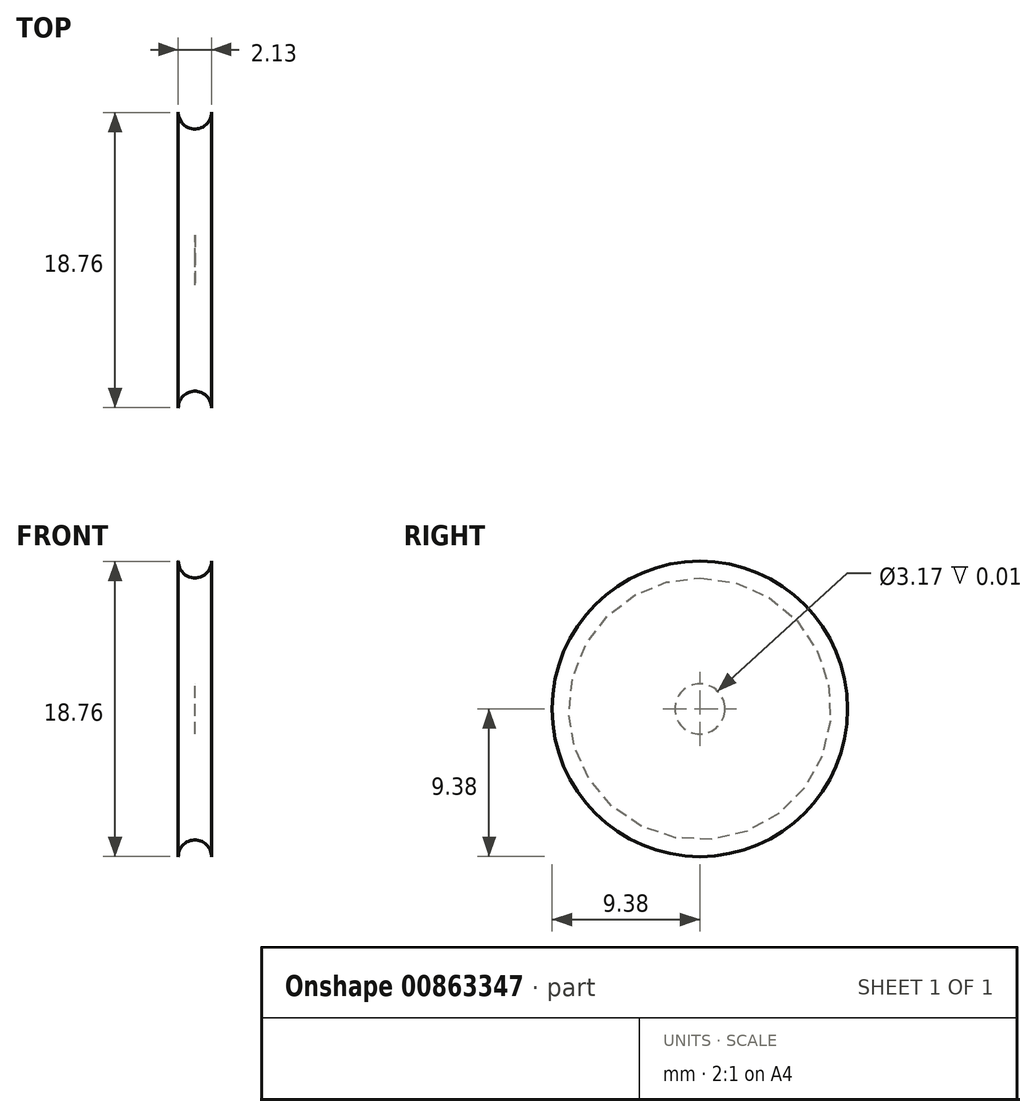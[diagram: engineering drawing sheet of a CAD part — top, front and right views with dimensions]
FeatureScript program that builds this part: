
annotation { "Feature Type Name" : "Feature", "Feature Type Description" : "" }
export const myFeature = defineFeature(function(context is Context, id is Id, definition is map)
    precondition{}
    {
        {
            var Q0;
            Q0=qCreatedBy(makeId("Front.planeOp"),FACE);
            var sketch = newSketch(context, id + "F0", { "sketchPlane" : qUnion([Q0])});
            skCircle(sketch, "E0", {"center": v(0, -0.08) * mm, "radius": 9.53 * mm});
            skLineSegment(sketch, "E1.bottom", {"start": v(-1.07, 0) * mm, "end": v(1.06, 0) * mm});
            skLineSegment(sketch, "E1.top", {"start": v(-1.07, 9.38) * mm, "end": v(1.06, 9.38) * mm});
            skLineSegment(sketch, "E1.left", {"start": v(-1.07, 0) * mm, "end": v(-1.07, 9.38) * mm});
            skLineSegment(sketch, "E1.right", {"start": v(1.06, 0) * mm, "end": v(1.06, 9.38) * mm});
            skCircle(sketch, "E2", {"center": v(0, 9.38) * mm, "radius": 1.06 * mm});
            skSolve(sketch);
        }
        {
            var Q0;
            {var subQ1=sQuery(id+"F0.wireOp",EDGE,"E1.bottom");Q0=makeQuery(id+"F0.imprint","IMPRINT",FACE,{"disambiguationData":[TD([[makeQuery(id+"F0.imprint","IMPRINT",EDGE,{"derivedFrom":subQ1}),1.0]])]});}
            var Q1;
            Q1=sQuery(id+"F0.wireOp",EDGE,"E1.bottom");
            revolve(context, id + "F1", {"surfaceOperationType" : NewSurfaceOperationType.NEW, "entities" : qUnion([Q0]), "axis" : qUnion([Q1]), "revolveType" : RevolveType.FULL});
        }
        {
            var Q0;
            Q0=qCreatedBy(makeId("Right.planeOp"),FACE);
            var sketch = newSketch(context, id + "F2", { "sketchPlane" : qUnion([Q0])});
            skCircle(sketch, "E3", {"center": v(0, 0) * mm, "radius": 1.59 * mm});
            skSolve(sketch);
        }
        {
            var Q0;
            Q0=qSketchRegion(id+"F2",true);
            extrude(context, id + "F3", {"entities" : qUnion([Q0]), "operationType" : NewBodyOperationType.REMOVE, "endBound" : BoundingType.SYMMETRIC, "depth" : 1 / 101.6 * mm, "offsetDistance" : 25 * mm});
        }
    });
